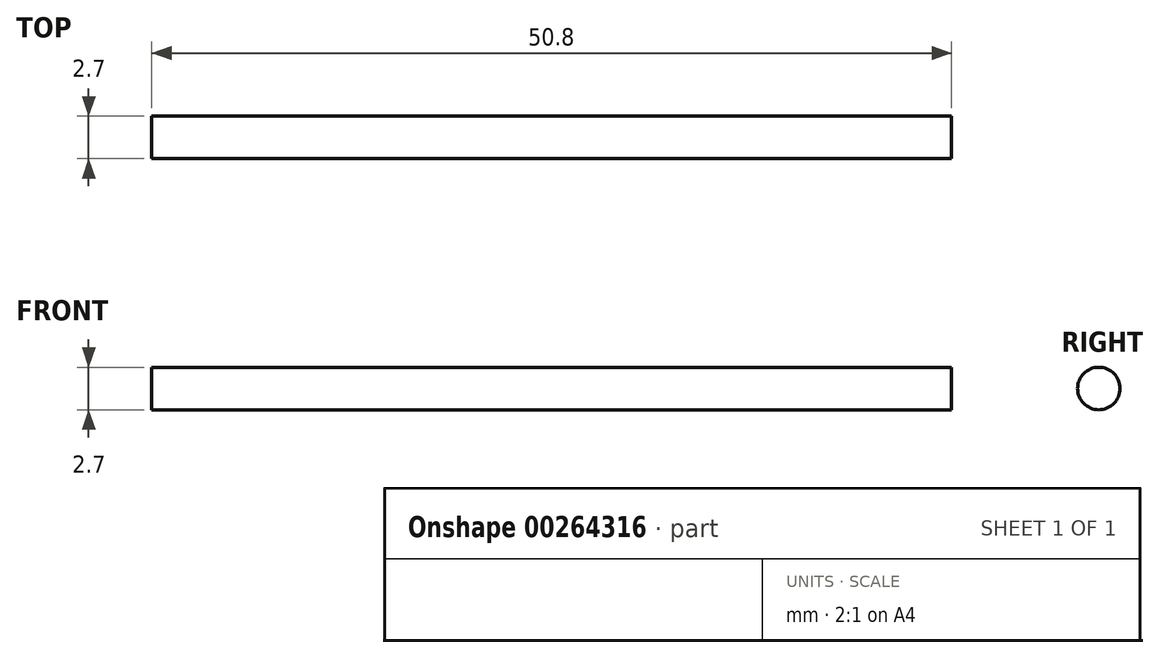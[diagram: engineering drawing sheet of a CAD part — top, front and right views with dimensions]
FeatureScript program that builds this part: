
annotation { "Feature Type Name" : "Feature", "Feature Type Description" : "" }
export const myFeature = defineFeature(function(context is Context, id is Id, definition is map)
    precondition{}
    {
        {
            var Q0;
            Q0=qCreatedBy(makeId("Right.planeOp"),FACE);
            var sketch = newSketch(context, id + "F0", { "sketchPlane" : qUnion([Q0])});
            skCircle(sketch, "E0", {"center": v(-37.4, 27.07) * mm, "radius": 1.35 * mm});
            skSolve(sketch);
        }
        {
            var Q0;
            Q0 = qSketchRegion(id + "F0", true);
            extrude(context, id + "F1", {"entities" : qUnion([Q0]), "depth" : 50.8 * mm});
        }
    });
